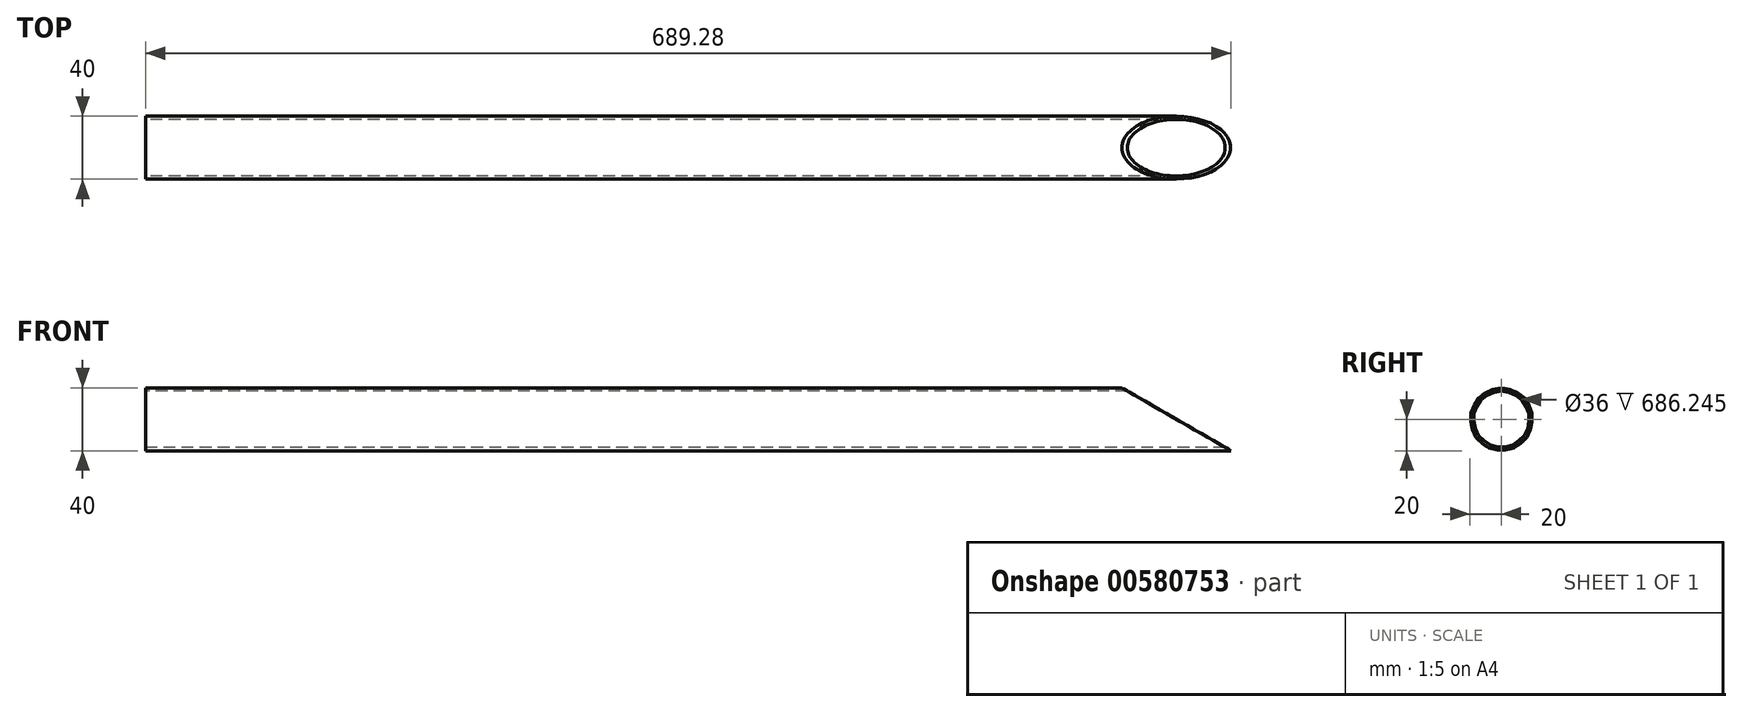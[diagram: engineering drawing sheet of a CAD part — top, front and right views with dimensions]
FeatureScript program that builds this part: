
annotation { "Feature Type Name" : "Feature", "Feature Type Description" : "" }
export const myFeature = defineFeature(function(context is Context, id is Id, definition is map)
    precondition{}
    {
        {
            var Q0;
            Q0=qCreatedBy(makeId("Right.planeOp"),FACE);
            var sketch = newSketch(context, id + "F0", { "sketchPlane" : qUnion([Q0])});
            skCircle(sketch, "E0", {"center": v(0, 0) * mm, "radius": 20 * mm});
            skCircle(sketch, "E1", {"center": v(0, 0) * mm, "radius": 18 * mm});
            skSolve(sketch);
        }
        {
            var Q0;
            Q0 = qSketchRegion(id + "F0", true);
            extrude(context, id + "F1", {"entities" : qUnion([Q0]), "depth" : 750 * mm, "offsetDistance" : 25 * mm});
        }
        {
            var Q0;
            Q0=qCreatedBy(makeId("Front.planeOp"),FACE);
            var sketch = newSketch(context, id + "F2", { "sketchPlane" : qUnion([Q0])});
            skLineSegment(sketch, "E2", {"start": v(689.28, -20) * mm, "end": v(620, 20) * mm});
            skLineSegment(sketch, "E3", {"start": v(620, 20) * mm, "end": v(689.28, 20) * mm});
            skLineSegment(sketch, "E4", {"start": v(689.28, 20) * mm, "end": v(689.28, -20) * mm, "construction": true});
            skLineSegment(sketch, "E5.bottom", {"start": v(689.28, 20) * mm, "end": v(803.44, 20) * mm});
            skLineSegment(sketch, "E5.top", {"start": v(689.28, -20) * mm, "end": v(803.44, -20) * mm});
            skLineSegment(sketch, "E5.right", {"start": v(803.44, 20) * mm, "end": v(803.44, -20) * mm});
            skSolve(sketch);
        }
        {
            var Q0;
            Q0 = qSketchRegion(id + "F2", true);
            extrude(context, id + "F3", {"entities" : qUnion([Q0]), "operationType" : NewBodyOperationType.REMOVE, "endBound" : BoundingType.THROUGH_ALL, "oppositeDirection" : true, "depth" : 25 * mm, "offsetDistance" : 25 * mm, "hasSecondDirection" : true, "secondDirectionBound" : SecondDirectionBoundingType.THROUGH_ALL, "secondDirectionOppositeDirection" : false, "secondDirectionDepth" : 25 * mm});
        }
    });
